# Revit family: Practibox_S_cofrecito_empotrado_12_módulos_réf_135041_a_135074
name_source: partatom
category: Equipement électrique
revit_build: Autodesk Revit 2018 (Build: 20170223_1515(x64)
units: mm (PartAtom-declared; Revit-internal decimal feet)

## family parameters
Basée sur le plan de construction = Non
Configuration du panneau = Deux colonnes, circuits au sein
Cote de connecteur circulaire = Utiliser le diamètre
Couper avec des vides une fois chargée = Non
Numéro OmniClass = 23.80.30.11.17
Partagée = Non
Point de calcul de pièce = Non
Titre OmniClass = Distribution Boards and Control Panels
Toujours verticalement = Oui
Type d'élément = Tableau de raccordement

## types (16) — shared parameters
Condiciones Generales de Uso = https://export.legrand.com
Fabricant = "Legrand"
URL = www.legrand.com
anchura = 328 mm  [stored 1.07612 ft]

## per-type parameters (varying)
| type | 1R | 2R | 3R | 4R | Altura | Bornas T | Ina | profundidad | puerta B 1 r | puerta B 2 r | puerta B 3 r | puerta B 4 r | puerta T 1 r | puerta T 2 r | puerta T 3 r | puerta T 4 r | puerta blanca | puerta transparencia | tamaño |
| Practibox_S_cofrecito_empotrado_12_módulos_135071 | Oui | Non | Non | Non | 235 mm  [stored 0.770997 ft] | 10 salidas Icc 6kA | 63 A | 102 mm | Non | Non | Non | Non | Oui | Non | Non | Non | Non | Oui | 1 fila |
| Practibox_S_cofrecito_empotrado_12_módulos_135061 | Oui | Non | Non | Non | 235 mm  [stored 0.770997 ft] | 10 salidas Icc 6kA | 63 A | 102 mm | Oui | Non | Non | Non | Non | Non | Non | Non | Oui | Non | 1 fila |
| Practibox_S_cofrecito_empotrado_12_módulos_135051 | Oui | Non | Non | Non | 235 mm  [stored 0.770997 ft] | 10 salidas Icc 6kA | 63 A | 102 mm | Non | Non | Non | Non | Oui | Non | Non | Non | Non | Oui | 1 fila |
| Practibox_S_cofrecito_empotrado_12_módulos_135041 | Oui | Non | Non | Non | 235 mm  [stored 0.770997 ft] | 10 salidas Icc 6kA | 63 A | 102 mm | Oui | Non | Non | Non | Non | Non | Non | Non | Oui | Non | 1 fila |
| Practibox_S_cofrecito_empotrado_24_módulos_135072 | Non | Oui | Non | Non | 385 mm  [stored 1.26312 ft] | 16 salidas Icc 6kA | 90 A | 103 mm  [stored 0.337927 ft] | Non | Non | Non | Non | Non | Oui | Non | Non | Non | Oui | 2 fila |
| Practibox_S_cofrecito_empotrado_24_módulos_135062 | Non | Oui | Non | Non | 385 mm  [stored 1.26312 ft] | 16 salidas Icc 6kA | 90 A | 103 mm  [stored 0.337927 ft] | Non | Oui | Non | Non | Non | Non | Non | Non | Oui | Non | 2 fila |
| Practibox_S_cofrecito_empotrado_24_módulos_135042 | Non | Oui | Non | Non | 385 mm  [stored 1.26312 ft] | 16 salidas Icc 6kA | 90 A | 103 mm  [stored 0.337927 ft] | Non | Oui | Non | Non | Non | Non | Non | Non | Oui | Non | 2 fila |
| Practibox_S_cofrecito_empotrado_24_módulos_135052 | Non | Oui | Non | Non | 385 mm  [stored 1.26312 ft] | 16 salidas Icc 6kA | 90 A | 103 mm  [stored 0.337927 ft] | Non | Non | Non | Non | Non | Oui | Non | Non | Non | Oui | 2 fila |
| Practibox_S_cofrecito_empotrado_36_módulos_135073 | Non | Non | Oui | Non | 535 mm  [stored 1.75525 ft] | 24 salidas Icc 6kA | 90 A | 103 mm  [stored 0.337927 ft] | Non | Non | Non | Non | Non | Non | Oui | Non | Non | Oui | 3 fila |
| Practibox_S_cofrecito_empotrado_48_módulos_135064 | Non | Non | Non | Oui | 765 mm  [stored 2.50984 ft] | 32 salidas Icc 6kA | 90 A | 103 mm  [stored 0.337927 ft] | Non | Non | Non | Oui | Non | Non | Non | Non | Oui | Non | 4 fila |
| Practibox_S_cofrecito_empotrado_48_módulos_135074 | Non | Non | Non | Oui | 765 mm  [stored 2.50984 ft] | 32 salidas Icc 6kA | 90 A | 103 mm  [stored 0.337927 ft] | Non | Non | Non | Non | Non | Non | Non | Oui | Non | Oui | 4 fila |
| Practibox_S_cofrecito_empotrado_48_módulos_135054 | Non | Non | Non | Oui | 765 mm  [stored 2.50984 ft] | 32 salidas Icc 6kA | 90 A | 103 mm  [stored 0.337927 ft] | Non | Non | Non | Non | Non | Non | Non | Oui | Non | Oui | 4 fila |
| Practibox_S_cofrecito_empotrado_48_módulos_135044 | Non | Non | Non | Oui | 765 mm  [stored 2.50984 ft] | 32 salidas Icc 6kA | 90 A | 103 mm  [stored 0.337927 ft] | Non | Non | Non | Oui | Non | Non | Non | Non | Oui | Non | 4 fila |
| Practibox_S_cofrecito_empotrado_36_módulos_135063 | Non | Non | Oui | Non | 535 mm  [stored 1.75525 ft] | 24 salidas Icc 6kA | 90 A | 103 mm  [stored 0.337927 ft] | Non | Non | Oui | Non | Non | Non | Non | Non | Oui | Non | 3 fila |
| Practibox_S_cofrecito_empotrado_36_módulos_135053 | Non | Non | Oui | Non | 535 mm  [stored 1.75525 ft] | 24 salidas Icc 6kA | 90 A | 103 mm  [stored 0.337927 ft] | Non | Non | Non | Non | Non | Non | Oui | Non | Non | Oui | 3 fila |
| Practibox_S_cofrecito_empotrado_36_módulos_135043 | Non | Non | Oui | Non | 535 mm  [stored 1.75525 ft] | 24 salidas Icc 6kA | 90 A | 103 mm  [stored 0.337927 ft] | Non | Non | Non | Non | Non | Non | Oui | Non | Non | Oui | 3 fila |

note: column(s) folded — value = type name in every type: Description

note: [stored X ft] marks values corroborated as IEEE doubles in the binary element streams (Revit-internal decimal feet)
